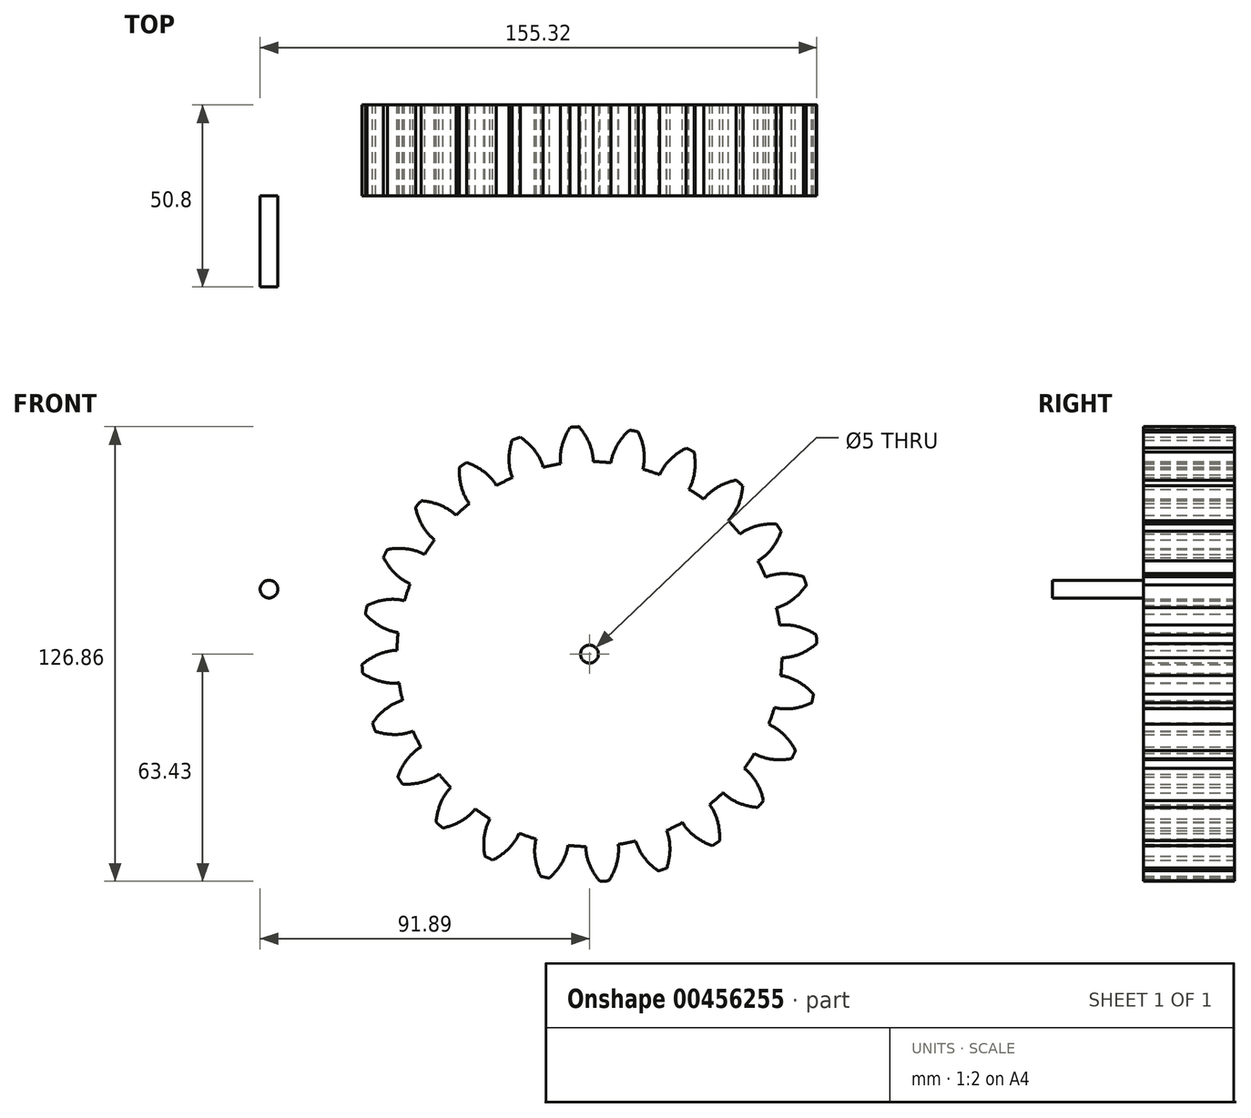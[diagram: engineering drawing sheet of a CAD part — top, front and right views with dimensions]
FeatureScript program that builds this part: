
annotation { "Feature Type Name" : "Feature", "Feature Type Description" : "" }
export const myFeature = defineFeature(function(context is Context, id is Id, definition is map)
    precondition{}
    {
        {
            var Q0;
            Q0=qCreatedBy(makeId("Front.planeOp"),FACE);
            var sketch = newSketch(context, id + "F0", { "sketchPlane" : qUnion([Q0])});
            skCircle(sketch, "E0", {"center": v(0, 0) * mm, "radius": 63.5 * mm, "construction": true});
            skCircle(sketch, "E1", {"center": v(0, 0) * mm, "radius": 58.67 * mm, "construction": true});
            skCircle(sketch, "E2", {"center": v(0, 0) * mm, "radius": 53.72 * mm});
            skLineSegment(sketch, "E3", {"start": v(0, 0) * mm, "end": v(0, 94.25) * mm, "construction": true});
            skLineSegment(sketch, "E4", {"start": v(0, 0) * mm, "end": v(-6.18, 94.25) * mm, "construction": true});
            skLineSegment(sketch, "E5", {"start": v(0, 58.67) * mm, "end": v(-72.33, 58.67) * mm, "construction": true});
            skLineSegment(sketch, "E6", {"start": v(0, 58.67) * mm, "end": v(-68.29, 33.82) * mm, "construction": true});
            skCircle(sketch, "E7", {"center": v(0, 0) * mm, "radius": 55.14 * mm, "construction": true});
            skCircle(sketch, "E8", {"center": v(0, 58.67) * mm, "radius": 14.6 * mm, "construction": true});
            skCircle(sketch, "E9", {"center": v(-13.57, 53.44) * mm, "radius": 14.6 * mm, "construction": true});
            skArc(sketch, "E10", {"start": v(0, 58.67) * mm, "mid": v(-1.27, 61.17) * mm, "end": v(-2.92, 63.43) * mm});
            skArc(sketch, "E11", {"start": v(1.03, 53.71) * mm, "mid": v(0.75, 56.24) * mm, "end": v(0, 58.67) * mm});
            skArc(sketch, "E12.MirrorCS", {"start": v(-7.66, 58.17) * mm, "mid": v(-6.72, 60.81) * mm, "end": v(-5.38, 63.27) * mm});
            skArc(sketch, "E13.MirrorCS", {"start": v(-8.03, 53.12) * mm, "mid": v(-8.08, 55.66) * mm, "end": v(-7.66, 58.17) * mm});
            skArc(sketch, "E14", {"start": v(-2.92, 63.43) * mm, "mid": v(-4.15, 63.38) * mm, "end": v(-5.38, 63.27) * mm});
            skSolve(sketch);
        }
        {
            var Q0;
            {var subQ0=sQuery(id+"F0.wireOp",EDGE,"E2");var subQ1=makeQuery(id+"F0.imprint","INTERSECT",VERTEX,{"derivedFrom":[subQ0,sQuery(id+"F0.wireOp",EDGE,"E11")]});Q0=makeQuery(id+"F0.imprint","IMPRINT",FACE,{"disambiguationData":[TD([[makeQuery(id+"F0.imprint","IMPRINT",EDGE,{"disambiguationData":[TD([[subQ1,-1.0]])],"derivedFrom":subQ0}),1.0]])]});}
            var Q1;
            Q1=makeQuery(id+"F0.imprint","IMPRINT",FACE,{"disambiguationData":[TD([[makeQuery(id+"F0.imprint","IMPRINT",EDGE,{"derivedFrom":sQuery(id+"F0.wireOp",EDGE,"E10")}),1.0]])]});
            extrude(context, id + "F1", {"entities" : qUnion([Q0, Q1]), "depth" : 25.4 * mm});
        }
        {
            var Q0;
            Q0=makeQuery(id+"F1.opExtrude","SWEPT_BODY",BODY,{"disambiguationData":[OSD([sQuery(id+"F0.wireOp",EDGE,"E2"),sQuery(id+"F0.wireOp",EDGE,"E10"),sQuery(id+"F0.wireOp",EDGE,"E11"),sQuery(id+"F0.wireOp",EDGE,"E12.MirrorCS"),sQuery(id+"F0.wireOp",EDGE,"E13.MirrorCS"),sQuery(id+"F0.wireOp",EDGE,"E14")])]});
            var Q1;
            Q1=makeQuery(id+"F1.opExtrude","SWEPT_FACE",FACE,{"disambiguationData":[OSD([sQuery(id+"F0.wireOp",EDGE,"E2")])]});
            circularPattern(context, id + "F2", {"entities" : qUnion([Q0]), "axis" : qUnion([Q1]), "angle" : 15 * degree, "instanceCount" : 24});
        }
        {
            var Q0;
            Q0=makeQuery(id+"F2.opPattern","COPY",BODY,{"derivedFrom":makeQuery(id+"F1.opExtrude","SWEPT_BODY",BODY,{"disambiguationData":[OSD([sQuery(id+"F0.wireOp",EDGE,"E2"),sQuery(id+"F0.wireOp",EDGE,"E10"),sQuery(id+"F0.wireOp",EDGE,"E11"),sQuery(id+"F0.wireOp",EDGE,"E12.MirrorCS"),sQuery(id+"F0.wireOp",EDGE,"E13.MirrorCS"),sQuery(id+"F0.wireOp",EDGE,"E14")])]}),"instanceName":"21"});
            var Q1;
            Q1=makeQuery(id+"F2.opPattern","COPY",BODY,{"derivedFrom":makeQuery(id+"F1.opExtrude","SWEPT_BODY",BODY,{"disambiguationData":[OSD([sQuery(id+"F0.wireOp",EDGE,"E2"),sQuery(id+"F0.wireOp",EDGE,"E10"),sQuery(id+"F0.wireOp",EDGE,"E11"),sQuery(id+"F0.wireOp",EDGE,"E12.MirrorCS"),sQuery(id+"F0.wireOp",EDGE,"E13.MirrorCS"),sQuery(id+"F0.wireOp",EDGE,"E14")])]}),"instanceName":"2"});
            var Q2;
            Q2=makeQuery(id+"F2.opPattern","COPY",BODY,{"derivedFrom":makeQuery(id+"F1.opExtrude","SWEPT_BODY",BODY,{"disambiguationData":[OSD([sQuery(id+"F0.wireOp",EDGE,"E2"),sQuery(id+"F0.wireOp",EDGE,"E10"),sQuery(id+"F0.wireOp",EDGE,"E11"),sQuery(id+"F0.wireOp",EDGE,"E12.MirrorCS"),sQuery(id+"F0.wireOp",EDGE,"E13.MirrorCS"),sQuery(id+"F0.wireOp",EDGE,"E14")])]}),"instanceName":"11"});
            var Q3;
            Q3=makeQuery(id+"F2.opPattern","COPY",BODY,{"derivedFrom":makeQuery(id+"F1.opExtrude","SWEPT_BODY",BODY,{"disambiguationData":[OSD([sQuery(id+"F0.wireOp",EDGE,"E2"),sQuery(id+"F0.wireOp",EDGE,"E10"),sQuery(id+"F0.wireOp",EDGE,"E11"),sQuery(id+"F0.wireOp",EDGE,"E12.MirrorCS"),sQuery(id+"F0.wireOp",EDGE,"E13.MirrorCS"),sQuery(id+"F0.wireOp",EDGE,"E14")])]}),"instanceName":"20"});
            var Q4;
            Q4=makeQuery(id+"F2.opPattern","COPY",BODY,{"derivedFrom":makeQuery(id+"F1.opExtrude","SWEPT_BODY",BODY,{"disambiguationData":[OSD([sQuery(id+"F0.wireOp",EDGE,"E2"),sQuery(id+"F0.wireOp",EDGE,"E10"),sQuery(id+"F0.wireOp",EDGE,"E11"),sQuery(id+"F0.wireOp",EDGE,"E12.MirrorCS"),sQuery(id+"F0.wireOp",EDGE,"E13.MirrorCS"),sQuery(id+"F0.wireOp",EDGE,"E14")])]}),"instanceName":"19"});
            var Q5;
            Q5=makeQuery(id+"F2.opPattern","COPY",BODY,{"derivedFrom":makeQuery(id+"F1.opExtrude","SWEPT_BODY",BODY,{"disambiguationData":[OSD([sQuery(id+"F0.wireOp",EDGE,"E2"),sQuery(id+"F0.wireOp",EDGE,"E10"),sQuery(id+"F0.wireOp",EDGE,"E11"),sQuery(id+"F0.wireOp",EDGE,"E12.MirrorCS"),sQuery(id+"F0.wireOp",EDGE,"E13.MirrorCS"),sQuery(id+"F0.wireOp",EDGE,"E14")])]}),"instanceName":"1"});
            var Q6;
            Q6=makeQuery(id+"F2.opPattern","COPY",BODY,{"derivedFrom":makeQuery(id+"F1.opExtrude","SWEPT_BODY",BODY,{"disambiguationData":[OSD([sQuery(id+"F0.wireOp",EDGE,"E2"),sQuery(id+"F0.wireOp",EDGE,"E10"),sQuery(id+"F0.wireOp",EDGE,"E11"),sQuery(id+"F0.wireOp",EDGE,"E12.MirrorCS"),sQuery(id+"F0.wireOp",EDGE,"E13.MirrorCS"),sQuery(id+"F0.wireOp",EDGE,"E14")])]}),"instanceName":"15"});
            var Q7;
            Q7=makeQuery(id+"F1.opExtrude","SWEPT_BODY",BODY,{"disambiguationData":[OSD([sQuery(id+"F0.wireOp",EDGE,"E2"),sQuery(id+"F0.wireOp",EDGE,"E10"),sQuery(id+"F0.wireOp",EDGE,"E11"),sQuery(id+"F0.wireOp",EDGE,"E12.MirrorCS"),sQuery(id+"F0.wireOp",EDGE,"E13.MirrorCS"),sQuery(id+"F0.wireOp",EDGE,"E14")])]});
            var Q8;
            Q8=makeQuery(id+"F2.opPattern","COPY",BODY,{"derivedFrom":makeQuery(id+"F1.opExtrude","SWEPT_BODY",BODY,{"disambiguationData":[OSD([sQuery(id+"F0.wireOp",EDGE,"E2"),sQuery(id+"F0.wireOp",EDGE,"E10"),sQuery(id+"F0.wireOp",EDGE,"E11"),sQuery(id+"F0.wireOp",EDGE,"E12.MirrorCS"),sQuery(id+"F0.wireOp",EDGE,"E13.MirrorCS"),sQuery(id+"F0.wireOp",EDGE,"E14")])]}),"instanceName":"7"});
            var Q9;
            Q9=makeQuery(id+"F2.opPattern","COPY",BODY,{"derivedFrom":makeQuery(id+"F1.opExtrude","SWEPT_BODY",BODY,{"disambiguationData":[OSD([sQuery(id+"F0.wireOp",EDGE,"E2"),sQuery(id+"F0.wireOp",EDGE,"E10"),sQuery(id+"F0.wireOp",EDGE,"E11"),sQuery(id+"F0.wireOp",EDGE,"E12.MirrorCS"),sQuery(id+"F0.wireOp",EDGE,"E13.MirrorCS"),sQuery(id+"F0.wireOp",EDGE,"E14")])]}),"instanceName":"22"});
            var Q10;
            Q10=makeQuery(id+"F2.opPattern","COPY",BODY,{"derivedFrom":makeQuery(id+"F1.opExtrude","SWEPT_BODY",BODY,{"disambiguationData":[OSD([sQuery(id+"F0.wireOp",EDGE,"E2"),sQuery(id+"F0.wireOp",EDGE,"E10"),sQuery(id+"F0.wireOp",EDGE,"E11"),sQuery(id+"F0.wireOp",EDGE,"E12.MirrorCS"),sQuery(id+"F0.wireOp",EDGE,"E13.MirrorCS"),sQuery(id+"F0.wireOp",EDGE,"E14")])]}),"instanceName":"16"});
            var Q11;
            Q11=makeQuery(id+"F2.opPattern","COPY",BODY,{"derivedFrom":makeQuery(id+"F1.opExtrude","SWEPT_BODY",BODY,{"disambiguationData":[OSD([sQuery(id+"F0.wireOp",EDGE,"E2"),sQuery(id+"F0.wireOp",EDGE,"E10"),sQuery(id+"F0.wireOp",EDGE,"E11"),sQuery(id+"F0.wireOp",EDGE,"E12.MirrorCS"),sQuery(id+"F0.wireOp",EDGE,"E13.MirrorCS"),sQuery(id+"F0.wireOp",EDGE,"E14")])]}),"instanceName":"4"});
            var Q12;
            Q12=makeQuery(id+"F2.opPattern","COPY",BODY,{"derivedFrom":makeQuery(id+"F1.opExtrude","SWEPT_BODY",BODY,{"disambiguationData":[OSD([sQuery(id+"F0.wireOp",EDGE,"E2"),sQuery(id+"F0.wireOp",EDGE,"E10"),sQuery(id+"F0.wireOp",EDGE,"E11"),sQuery(id+"F0.wireOp",EDGE,"E12.MirrorCS"),sQuery(id+"F0.wireOp",EDGE,"E13.MirrorCS"),sQuery(id+"F0.wireOp",EDGE,"E14")])]}),"instanceName":"12"});
            var Q13;
            Q13=makeQuery(id+"F2.opPattern","COPY",BODY,{"derivedFrom":makeQuery(id+"F1.opExtrude","SWEPT_BODY",BODY,{"disambiguationData":[OSD([sQuery(id+"F0.wireOp",EDGE,"E2"),sQuery(id+"F0.wireOp",EDGE,"E10"),sQuery(id+"F0.wireOp",EDGE,"E11"),sQuery(id+"F0.wireOp",EDGE,"E12.MirrorCS"),sQuery(id+"F0.wireOp",EDGE,"E13.MirrorCS"),sQuery(id+"F0.wireOp",EDGE,"E14")])]}),"instanceName":"13"});
            var Q14;
            Q14=makeQuery(id+"F2.opPattern","COPY",BODY,{"derivedFrom":makeQuery(id+"F1.opExtrude","SWEPT_BODY",BODY,{"disambiguationData":[OSD([sQuery(id+"F0.wireOp",EDGE,"E2"),sQuery(id+"F0.wireOp",EDGE,"E10"),sQuery(id+"F0.wireOp",EDGE,"E11"),sQuery(id+"F0.wireOp",EDGE,"E12.MirrorCS"),sQuery(id+"F0.wireOp",EDGE,"E13.MirrorCS"),sQuery(id+"F0.wireOp",EDGE,"E14")])]}),"instanceName":"9"});
            var Q15;
            Q15=makeQuery(id+"F2.opPattern","COPY",BODY,{"derivedFrom":makeQuery(id+"F1.opExtrude","SWEPT_BODY",BODY,{"disambiguationData":[OSD([sQuery(id+"F0.wireOp",EDGE,"E2"),sQuery(id+"F0.wireOp",EDGE,"E10"),sQuery(id+"F0.wireOp",EDGE,"E11"),sQuery(id+"F0.wireOp",EDGE,"E12.MirrorCS"),sQuery(id+"F0.wireOp",EDGE,"E13.MirrorCS"),sQuery(id+"F0.wireOp",EDGE,"E14")])]}),"instanceName":"8"});
            var Q16;
            Q16=makeQuery(id+"F2.opPattern","COPY",BODY,{"derivedFrom":makeQuery(id+"F1.opExtrude","SWEPT_BODY",BODY,{"disambiguationData":[OSD([sQuery(id+"F0.wireOp",EDGE,"E2"),sQuery(id+"F0.wireOp",EDGE,"E10"),sQuery(id+"F0.wireOp",EDGE,"E11"),sQuery(id+"F0.wireOp",EDGE,"E12.MirrorCS"),sQuery(id+"F0.wireOp",EDGE,"E13.MirrorCS"),sQuery(id+"F0.wireOp",EDGE,"E14")])]}),"instanceName":"10"});
            var Q17;
            Q17=makeQuery(id+"F2.opPattern","COPY",BODY,{"derivedFrom":makeQuery(id+"F1.opExtrude","SWEPT_BODY",BODY,{"disambiguationData":[OSD([sQuery(id+"F0.wireOp",EDGE,"E2"),sQuery(id+"F0.wireOp",EDGE,"E10"),sQuery(id+"F0.wireOp",EDGE,"E11"),sQuery(id+"F0.wireOp",EDGE,"E12.MirrorCS"),sQuery(id+"F0.wireOp",EDGE,"E13.MirrorCS"),sQuery(id+"F0.wireOp",EDGE,"E14")])]}),"instanceName":"6"});
            var Q18;
            Q18=makeQuery(id+"F2.opPattern","COPY",BODY,{"derivedFrom":makeQuery(id+"F1.opExtrude","SWEPT_BODY",BODY,{"disambiguationData":[OSD([sQuery(id+"F0.wireOp",EDGE,"E2"),sQuery(id+"F0.wireOp",EDGE,"E10"),sQuery(id+"F0.wireOp",EDGE,"E11"),sQuery(id+"F0.wireOp",EDGE,"E12.MirrorCS"),sQuery(id+"F0.wireOp",EDGE,"E13.MirrorCS"),sQuery(id+"F0.wireOp",EDGE,"E14")])]}),"instanceName":"14"});
            var Q19;
            Q19=makeQuery(id+"F2.opPattern","COPY",BODY,{"derivedFrom":makeQuery(id+"F1.opExtrude","SWEPT_BODY",BODY,{"disambiguationData":[OSD([sQuery(id+"F0.wireOp",EDGE,"E2"),sQuery(id+"F0.wireOp",EDGE,"E10"),sQuery(id+"F0.wireOp",EDGE,"E11"),sQuery(id+"F0.wireOp",EDGE,"E12.MirrorCS"),sQuery(id+"F0.wireOp",EDGE,"E13.MirrorCS"),sQuery(id+"F0.wireOp",EDGE,"E14")])]}),"instanceName":"3"});
            var Q20;
            Q20=makeQuery(id+"F2.opPattern","COPY",BODY,{"derivedFrom":makeQuery(id+"F1.opExtrude","SWEPT_BODY",BODY,{"disambiguationData":[OSD([sQuery(id+"F0.wireOp",EDGE,"E2"),sQuery(id+"F0.wireOp",EDGE,"E10"),sQuery(id+"F0.wireOp",EDGE,"E11"),sQuery(id+"F0.wireOp",EDGE,"E12.MirrorCS"),sQuery(id+"F0.wireOp",EDGE,"E13.MirrorCS"),sQuery(id+"F0.wireOp",EDGE,"E14")])]}),"instanceName":"5"});
            var Q21;
            Q21=makeQuery(id+"F2.opPattern","COPY",BODY,{"derivedFrom":makeQuery(id+"F1.opExtrude","SWEPT_BODY",BODY,{"disambiguationData":[OSD([sQuery(id+"F0.wireOp",EDGE,"E2"),sQuery(id+"F0.wireOp",EDGE,"E10"),sQuery(id+"F0.wireOp",EDGE,"E11"),sQuery(id+"F0.wireOp",EDGE,"E12.MirrorCS"),sQuery(id+"F0.wireOp",EDGE,"E13.MirrorCS"),sQuery(id+"F0.wireOp",EDGE,"E14")])]}),"instanceName":"23"});
            var Q22;
            Q22=makeQuery(id+"F2.opPattern","COPY",BODY,{"derivedFrom":makeQuery(id+"F1.opExtrude","SWEPT_BODY",BODY,{"disambiguationData":[OSD([sQuery(id+"F0.wireOp",EDGE,"E2"),sQuery(id+"F0.wireOp",EDGE,"E10"),sQuery(id+"F0.wireOp",EDGE,"E11"),sQuery(id+"F0.wireOp",EDGE,"E12.MirrorCS"),sQuery(id+"F0.wireOp",EDGE,"E13.MirrorCS"),sQuery(id+"F0.wireOp",EDGE,"E14")])]}),"instanceName":"17"});
            var Q23;
            Q23=makeQuery(id+"F2.opPattern","COPY",BODY,{"derivedFrom":makeQuery(id+"F1.opExtrude","SWEPT_BODY",BODY,{"disambiguationData":[OSD([sQuery(id+"F0.wireOp",EDGE,"E2"),sQuery(id+"F0.wireOp",EDGE,"E10"),sQuery(id+"F0.wireOp",EDGE,"E11"),sQuery(id+"F0.wireOp",EDGE,"E12.MirrorCS"),sQuery(id+"F0.wireOp",EDGE,"E13.MirrorCS"),sQuery(id+"F0.wireOp",EDGE,"E14")])]}),"instanceName":"18"});
            booleanBodies(context, id + "F3", {"operationType" : BooleanOperationType.UNION, "tools" : qUnion([Q0, Q1, Q2, Q3, Q4, Q5, Q6, Q7, Q8, Q9, Q10, Q11, Q12, Q13, Q14, Q15, Q16, Q17, Q18, Q19, Q20, Q21, Q22, Q23])});
        }
        {
            var Q0;
            {var subQ0=makeQuery(id+"F1.opExtrude","CAP_FACE",FACE,{"disambiguationData":[OSD([sQuery(id+"F0.wireOp",EDGE,"E2"),sQuery(id+"F0.wireOp",EDGE,"E10"),sQuery(id+"F0.wireOp",EDGE,"E11"),sQuery(id+"F0.wireOp",EDGE,"E12.MirrorCS"),sQuery(id+"F0.wireOp",EDGE,"E13.MirrorCS"),sQuery(id+"F0.wireOp",EDGE,"E14")])],"isStart":false});Q0=makeQuery(id+"F3.opBoolean","MERGE",FACE,{"derivedFrom":[subQ0,makeQuery(id+"F2.opPattern","COPY",FACE,{"derivedFrom":subQ0,"instanceName":"1"}),makeQuery(id+"F2.opPattern","COPY",FACE,{"derivedFrom":subQ0,"instanceName":"2"}),makeQuery(id+"F2.opPattern","COPY",FACE,{"derivedFrom":subQ0,"instanceName":"3"}),makeQuery(id+"F2.opPattern","COPY",FACE,{"derivedFrom":subQ0,"instanceName":"4"}),makeQuery(id+"F2.opPattern","COPY",FACE,{"derivedFrom":subQ0,"instanceName":"5"}),makeQuery(id+"F2.opPattern","COPY",FACE,{"derivedFrom":subQ0,"instanceName":"6"}),makeQuery(id+"F2.opPattern","COPY",FACE,{"derivedFrom":subQ0,"instanceName":"7"}),makeQuery(id+"F2.opPattern","COPY",FACE,{"derivedFrom":subQ0,"instanceName":"8"}),makeQuery(id+"F2.opPattern","COPY",FACE,{"derivedFrom":subQ0,"instanceName":"9"}),makeQuery(id+"F2.opPattern","COPY",FACE,{"derivedFrom":subQ0,"instanceName":"10"}),makeQuery(id+"F2.opPattern","COPY",FACE,{"derivedFrom":subQ0,"instanceName":"11"}),makeQuery(id+"F2.opPattern","COPY",FACE,{"derivedFrom":subQ0,"instanceName":"12"}),makeQuery(id+"F2.opPattern","COPY",FACE,{"derivedFrom":subQ0,"instanceName":"13"}),makeQuery(id+"F2.opPattern","COPY",FACE,{"derivedFrom":subQ0,"instanceName":"14"}),makeQuery(id+"F2.opPattern","COPY",FACE,{"derivedFrom":subQ0,"instanceName":"15"}),makeQuery(id+"F2.opPattern","COPY",FACE,{"derivedFrom":subQ0,"instanceName":"16"}),makeQuery(id+"F2.opPattern","COPY",FACE,{"derivedFrom":subQ0,"instanceName":"17"}),makeQuery(id+"F2.opPattern","COPY",FACE,{"derivedFrom":subQ0,"instanceName":"18"}),makeQuery(id+"F2.opPattern","COPY",FACE,{"derivedFrom":subQ0,"instanceName":"19"}),makeQuery(id+"F2.opPattern","COPY",FACE,{"derivedFrom":subQ0,"instanceName":"20"}),makeQuery(id+"F2.opPattern","COPY",FACE,{"derivedFrom":subQ0,"instanceName":"21"}),makeQuery(id+"F2.opPattern","COPY",FACE,{"derivedFrom":subQ0,"instanceName":"22"}),makeQuery(id+"F2.opPattern","COPY",FACE,{"derivedFrom":subQ0,"instanceName":"23"})]});}
            var sketch = newSketch(context, id + "F4", { "sketchPlane" : qUnion([Q0])});
            skPoint(sketch, "E15", {"position": v(0, 0) * mm});
            skSolve(sketch);
        }
        {
            var Q0;
            Q0=sQuery(id+"F4.wireOp",VERTEX,"E15");
            var Q1;
            Q1=makeQuery(id+"F2.opPattern","COPY",BODY,{"derivedFrom":makeQuery(id+"F1.opExtrude","SWEPT_BODY",BODY,{"disambiguationData":[OSD([sQuery(id+"F0.wireOp",EDGE,"E2"),sQuery(id+"F0.wireOp",EDGE,"E10"),sQuery(id+"F0.wireOp",EDGE,"E11"),sQuery(id+"F0.wireOp",EDGE,"E12.MirrorCS"),sQuery(id+"F0.wireOp",EDGE,"E13.MirrorCS"),sQuery(id+"F0.wireOp",EDGE,"E14")])]}),"instanceName":"21"});
            hole(context, id + "F5", {"style" : HoleStyle.SIMPLE, "endStyle" : HoleEndStyle.THROUGH, "holeDiameter" : 5 * mm, "isTappedThrough" : true, "tappedDepth" : 12.7 * mm, "tapClearance" : 3, "startFromSketch" : true, "locations" : qUnion([Q0]), "scope" : qUnion([Q1])});
        }
        {
            var Q0;
            {var subQ0=makeQuery(id+"F1.opExtrude","CAP_FACE",FACE,{"disambiguationData":[OSD([sQuery(id+"F0.wireOp",EDGE,"E2"),sQuery(id+"F0.wireOp",EDGE,"E10"),sQuery(id+"F0.wireOp",EDGE,"E11"),sQuery(id+"F0.wireOp",EDGE,"E12.MirrorCS"),sQuery(id+"F0.wireOp",EDGE,"E13.MirrorCS"),sQuery(id+"F0.wireOp",EDGE,"E14")])],"isStart":false});Q0=makeQuery(id+"F3.opBoolean","MERGE",FACE,{"derivedFrom":[subQ0,makeQuery(id+"F2.opPattern","COPY",FACE,{"derivedFrom":subQ0,"instanceName":"1"}),makeQuery(id+"F2.opPattern","COPY",FACE,{"derivedFrom":subQ0,"instanceName":"2"}),makeQuery(id+"F2.opPattern","COPY",FACE,{"derivedFrom":subQ0,"instanceName":"3"}),makeQuery(id+"F2.opPattern","COPY",FACE,{"derivedFrom":subQ0,"instanceName":"4"}),makeQuery(id+"F2.opPattern","COPY",FACE,{"derivedFrom":subQ0,"instanceName":"5"}),makeQuery(id+"F2.opPattern","COPY",FACE,{"derivedFrom":subQ0,"instanceName":"6"}),makeQuery(id+"F2.opPattern","COPY",FACE,{"derivedFrom":subQ0,"instanceName":"7"}),makeQuery(id+"F2.opPattern","COPY",FACE,{"derivedFrom":subQ0,"instanceName":"8"}),makeQuery(id+"F2.opPattern","COPY",FACE,{"derivedFrom":subQ0,"instanceName":"9"}),makeQuery(id+"F2.opPattern","COPY",FACE,{"derivedFrom":subQ0,"instanceName":"10"}),makeQuery(id+"F2.opPattern","COPY",FACE,{"derivedFrom":subQ0,"instanceName":"11"}),makeQuery(id+"F2.opPattern","COPY",FACE,{"derivedFrom":subQ0,"instanceName":"12"}),makeQuery(id+"F2.opPattern","COPY",FACE,{"derivedFrom":subQ0,"instanceName":"13"}),makeQuery(id+"F2.opPattern","COPY",FACE,{"derivedFrom":subQ0,"instanceName":"14"}),makeQuery(id+"F2.opPattern","COPY",FACE,{"derivedFrom":subQ0,"instanceName":"15"}),makeQuery(id+"F2.opPattern","COPY",FACE,{"derivedFrom":subQ0,"instanceName":"16"}),makeQuery(id+"F2.opPattern","COPY",FACE,{"derivedFrom":subQ0,"instanceName":"17"}),makeQuery(id+"F2.opPattern","COPY",FACE,{"derivedFrom":subQ0,"instanceName":"18"}),makeQuery(id+"F2.opPattern","COPY",FACE,{"derivedFrom":subQ0,"instanceName":"19"}),makeQuery(id+"F2.opPattern","COPY",FACE,{"derivedFrom":subQ0,"instanceName":"20"}),makeQuery(id+"F2.opPattern","COPY",FACE,{"derivedFrom":subQ0,"instanceName":"21"}),makeQuery(id+"F2.opPattern","COPY",FACE,{"derivedFrom":subQ0,"instanceName":"22"}),makeQuery(id+"F2.opPattern","COPY",FACE,{"derivedFrom":subQ0,"instanceName":"23"})]});}
            var sketch = newSketch(context, id + "F6", { "sketchPlane" : qUnion([Q0])});
            skCircle(sketch, "E16", {"center": v(-89.43, 18.1) * mm, "radius": 2.47 * mm});
            skSolve(sketch);
        }
        {
            var Q0;
            Q0=makeQuery(id+"F6.imprint","IMPRINT",FACE,{"disambiguationData":[TD([[makeQuery(id+"F6.imprint","IMPRINT",EDGE,{"derivedFrom":sQuery(id+"F6.wireOp",EDGE,"E16")}),1.0]])]});
            extrude(context, id + "F7", {"entities" : qUnion([Q0]), "depth" : 25.4 * mm});
        }
    });
